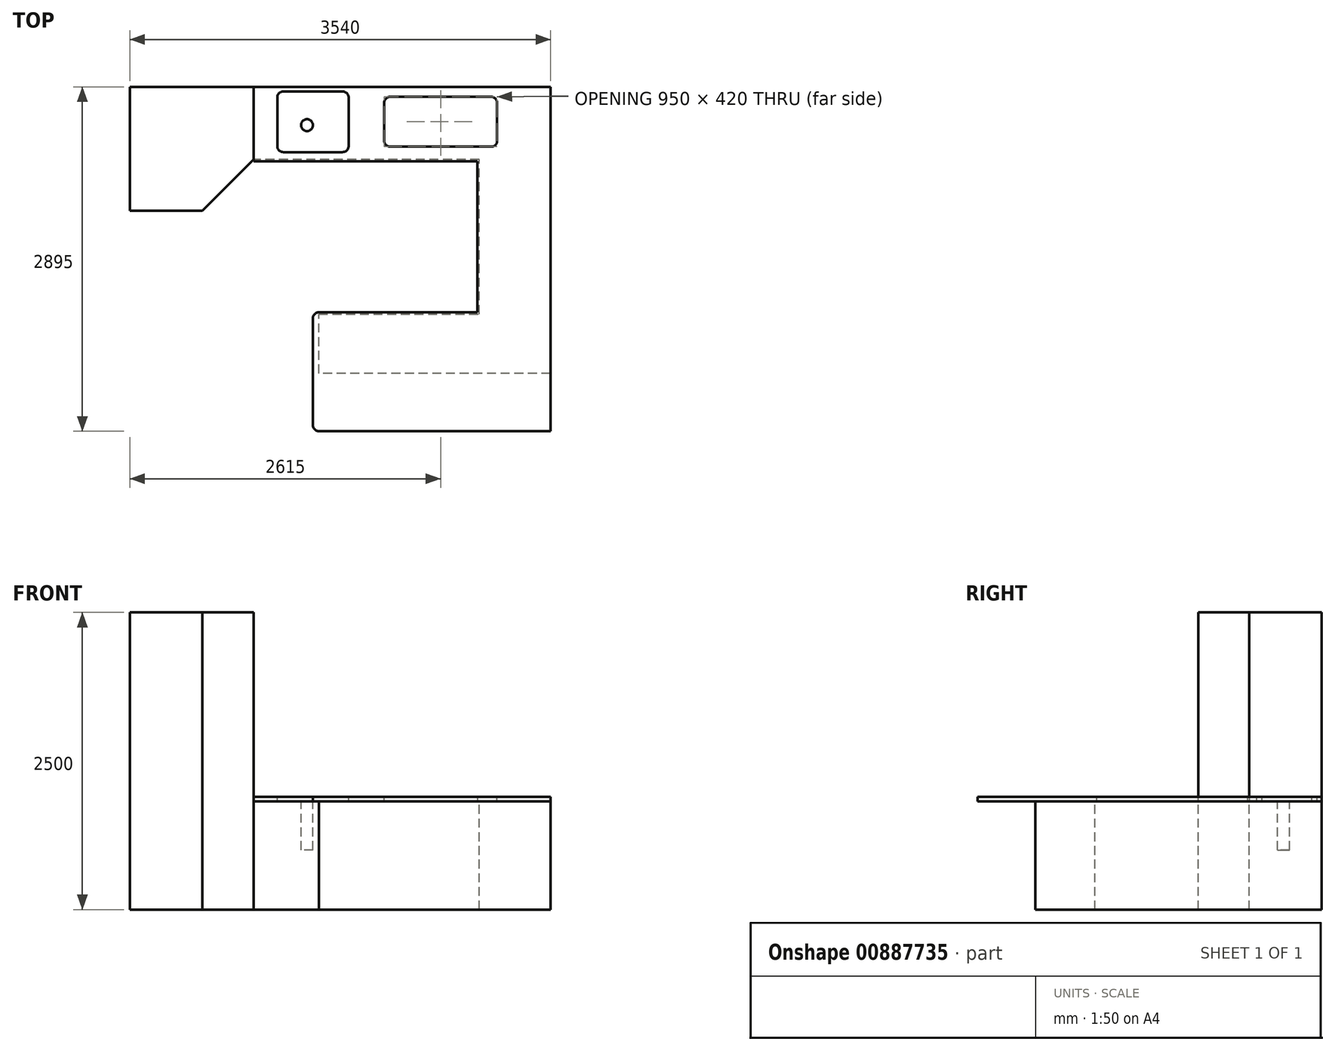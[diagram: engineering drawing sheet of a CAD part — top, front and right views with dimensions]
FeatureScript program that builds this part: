
annotation { "Feature Type Name" : "Feature", "Feature Type Description" : "" }
export const myFeature = defineFeature(function(context is Context, id is Id, definition is map)
    precondition{}
    {
        {
            var Q0;
            Q0=qCreatedBy(makeId("Top.planeOp"),FACE);
            var sketch = newSketch(context, id + "F0", { "sketchPlane" : qUnion([Q0])});
            skLineSegment(sketch, "E0.bottom", {"start": v(-624.7, -469.24) * mm, "end": v(415.3, -469.24) * mm});
            skLineSegment(sketch, "E0.top", {"start": v(-624.7, 570.76) * mm, "end": v(415.3, 570.76) * mm});
            skLineSegment(sketch, "E0.left", {"start": v(-624.7, -469.24) * mm, "end": v(-624.7, 570.76) * mm});
            skLineSegment(sketch, "E0.right", {"start": v(415.3, -469.24) * mm, "end": v(415.3, 570.76) * mm});
            skPoint(sketch, "E1.oppositeSnap0", {"position": v(-624.7, 50.76) * mm});
            skPoint(sketch, "E1.left.start.orphan", {"position": v(-624.7, 50.76) * mm});
            skSolve(sketch);
        }
        {
            var Q0;
            Q0 = qSketchRegion(id + "F0", true);
            extrude(context, id + "F1", {"entities" : qUnion([Q0]), "depth" : 2500 * mm, "offsetDistance" : 25 * mm});
        }
        {
            var Q0;
            Q0=makeQuery(id+"F1.opExtrude","SWEPT_EDGE",EDGE,{"disambiguationData":[OSD([sQuery(id+"F0.wireOp",EDGE,"E0.bottom"),sQuery(id+"F0.wireOp",EDGE,"E0.right")])]});
            chamfer(context, id + "F2", {"entities" : qUnion([Q0]), "width" : 430 * mm, "tangentPropagation" : true});
        }
        {
            var Q0;
            Q0=makeQuery(id+"F1.opExtrude","SWEPT_FACE",FACE,{"disambiguationData":[OSD([sQuery(id+"F0.wireOp",EDGE,"E0.right")])]});
            var sketch = newSketch(context, id + "F3", { "sketchPlane" : qUnion([Q0])});
            skLineSegment(sketch, "E2.bottom", {"start": v(570.76, 0) * mm, "end": v(-39.24, 0) * mm});
            skLineSegment(sketch, "E2.top", {"start": v(570.76, 910) * mm, "end": v(-39.24, 910) * mm});
            skLineSegment(sketch, "E2.left", {"start": v(570.76, 0) * mm, "end": v(570.76, 910) * mm});
            skLineSegment(sketch, "E2.right", {"start": v(-39.24, 0) * mm, "end": v(-39.24, 910) * mm});
            skSolve(sketch);
        }
        {
            var Q0;
            Q0=makeQuery(id+"F3.imprint","IMPRINT",FACE,{"disambiguationData":[TD([[makeQuery(id+"F3.imprint","IMPRINT",EDGE,{"derivedFrom":sQuery(id+"F3.wireOp",EDGE,"E2.bottom")}),1.0]])]});
            extrude(context, id + "F4", {"entities" : qUnion([Q0]), "operationType" : NewBodyOperationType.ADD, "depth" : 2500 * mm, "offsetDistance" : 25 * mm});
        }
        {
            var Q0;
            Q0=makeQuery(id+"F4.opExtrude","SWEPT_FACE",FACE,{"disambiguationData":[OSD([sQuery(id+"F3.wireOp",EDGE,"E2.right")])]});
            var sketch = newSketch(context, id + "F5", { "sketchPlane" : qUnion([Q0])});
            skLineSegment(sketch, "E3.bottom", {"start": v(2915.3, 0) * mm, "end": v(2315.3, 0) * mm});
            skLineSegment(sketch, "E3.top", {"start": v(2915.3, 910) * mm, "end": v(2315.3, 910) * mm});
            skLineSegment(sketch, "E3.left", {"start": v(2915.3, 0) * mm, "end": v(2915.3, 910) * mm});
            skLineSegment(sketch, "E3.right", {"start": v(2315.3, 0) * mm, "end": v(2315.3, 910) * mm});
            skSolve(sketch);
        }
        {
            var Q0;
            Q0=makeQuery(id+"F5.imprint","IMPRINT",FACE,{"disambiguationData":[TD([[makeQuery(id+"F5.imprint","IMPRINT",EDGE,{"derivedFrom":sQuery(id+"F5.wireOp",EDGE,"E3.bottom")}),-1.0]])]});
            extrude(context, id + "F6", {"entities" : qUnion([Q0]), "operationType" : NewBodyOperationType.ADD, "depth" : 1800 * mm, "offsetDistance" : 25 * mm});
        }
        {
            var Q0;
            Q0=makeQuery(id+"F6.opExtrude","SWEPT_FACE",FACE,{"disambiguationData":[OSD([sQuery(id+"F5.wireOp",EDGE,"E3.right")])]});
            var sketch = newSketch(context, id + "F7", { "sketchPlane" : qUnion([Q0])});
            skLineSegment(sketch, "E4.bottom", {"start": v(1839.24, 0) * mm, "end": v(1339.24, 0) * mm});
            skLineSegment(sketch, "E4.top", {"start": v(1839.24, 910) * mm, "end": v(1339.24, 910) * mm});
            skLineSegment(sketch, "E4.left", {"start": v(1839.24, 0) * mm, "end": v(1839.24, 910) * mm});
            skLineSegment(sketch, "E4.right", {"start": v(1339.24, 0) * mm, "end": v(1339.24, 910) * mm});
            skSolve(sketch);
        }
        {
            var Q0;
            Q0=makeQuery(id+"F7.imprint","IMPRINT",FACE,{"disambiguationData":[TD([[makeQuery(id+"F7.imprint","IMPRINT",EDGE,{"derivedFrom":sQuery(id+"F7.wireOp",EDGE,"E4.bottom")}),-1.0]])]});
            extrude(context, id + "F8", {"entities" : qUnion([Q0]), "operationType" : NewBodyOperationType.ADD, "depth" : 1400 * mm, "offsetDistance" : 25 * mm});
        }
        {
            var Q0;
            Q0=makeQuery(id+"F8.boolean.opBoolean","MERGE",FACE,{"derivedFrom":[makeQuery(id+"F6.boolean.opBoolean","MERGE",FACE,{"derivedFrom":[makeQuery(id+"F4.opExtrude","SWEPT_FACE",FACE,{"disambiguationData":[OSD([sQuery(id+"F3.wireOp",EDGE,"E2.top")])]}),makeQuery(id+"F6.opExtrude","SWEPT_FACE",FACE,{"disambiguationData":[OSD([sQuery(id+"F5.wireOp",EDGE,"E3.top")])]})]}),makeQuery(id+"F8.opExtrude","SWEPT_FACE",FACE,{"disambiguationData":[OSD([sQuery(id+"F7.wireOp",EDGE,"E4.top")])]})]});
            var sketch = newSketch(context, id + "F9", { "sketchPlane" : qUnion([Q0])});
            skLineSegment(sketch, "E5", {"start": v(2915.3, -1839.24) * mm, "end": v(2915.3, -2324.24) * mm});
            skLineSegment(sketch, "E6", {"start": v(2915.3, -2324.24) * mm, "end": v(915.3, -2324.24) * mm});
            skLineSegment(sketch, "E7", {"start": v(915.3, -2324.24) * mm, "end": v(915.3, -1339.24) * mm});
            skLineSegment(sketch, "E8", {"start": v(915.3, -1339.24) * mm, "end": v(915.3, -1324.24) * mm});
            skLineSegment(sketch, "E9", {"start": v(915.3, -1324.24) * mm, "end": v(2300.3, -1324.24) * mm});
            skLineSegment(sketch, "E10", {"start": v(2300.3, -1324.24) * mm, "end": v(2300.3, -54.24) * mm});
            skLineSegment(sketch, "E11", {"start": v(2300.3, -54.24) * mm, "end": v(415.3, -54.24) * mm});
            skLineSegment(sketch, "E12", {"start": v(415.3, -54.24) * mm, "end": v(415.3, 570.76) * mm});
            skLineSegment(sketch, "E13", {"start": v(415.3, 570.76) * mm, "end": v(2915.3, 570.76) * mm});
            skLineSegment(sketch, "E14", {"start": v(2915.3, 570.76) * mm, "end": v(2915.3, -1839.24) * mm});
            skSolve(sketch);
        }
        {
            var Q0;
            Q0 = qSketchRegion(id + "F9", true);
            extrude(context, id + "F10", {"entities" : qUnion([Q0]), "depth" : 38 * mm, "offsetDistance" : 25 * mm});
        }
        {
            var Q0;
            Q0=makeQuery(id+"F10.opExtrude","SWEPT_EDGE",EDGE,{"disambiguationData":[OSD([sQuery(id+"F9.wireOp",EDGE,"E8"),sQuery(id+"F9.wireOp",EDGE,"E9")])]});
            var Q1;
            Q1=makeQuery(id+"F10.opExtrude","SWEPT_EDGE",EDGE,{"disambiguationData":[OSD([sQuery(id+"F9.wireOp",EDGE,"E6"),sQuery(id+"F9.wireOp",EDGE,"E7")])]});
            fillet(context, id + "F11", {"entities" : qUnion([Q0, Q1]), "radius" : 50 * mm, "tangentPropagation" : true, "allowEdgeOverflow" : false});
        }
        {
            var Q0;
            Q0=makeQuery(id+"F8.opExtrude","CAP_FACE",FACE,{"disambiguationData":[OSD([sQuery(id+"F7.wireOp",EDGE,"E4.bottom"),sQuery(id+"F7.wireOp",EDGE,"E4.top"),sQuery(id+"F7.wireOp",EDGE,"E4.left"),sQuery(id+"F7.wireOp",EDGE,"E4.right")])],"isStart":false});
            var sketch = newSketch(context, id + "F12", { "sketchPlane" : qUnion([Q0])});
            skLineSegment(sketch, "E15.bottom", {"start": v(1839.24, 0) * mm, "end": v(1339.24, 0) * mm});
            skLineSegment(sketch, "E15.top", {"start": v(1839.24, 910) * mm, "end": v(1339.24, 910) * mm});
            skLineSegment(sketch, "E15.left", {"start": v(1839.24, 0) * mm, "end": v(1839.24, 910) * mm});
            skLineSegment(sketch, "E15.right", {"start": v(1339.24, 0) * mm, "end": v(1339.24, 910) * mm});
            skSolve(sketch);
        }
        {
            var Q0;
            Q0 = qSketchRegion(id + "F12", true);
            extrude(context, id + "F13", {"entities" : qUnion([Q0]), "operationType" : NewBodyOperationType.REMOVE, "oppositeDirection" : true, "depth" : 50 * mm, "offsetDistance" : 25 * mm});
        }
        {
            var Q0;
            Q0=makeQuery(id+"F8.boolean.opBoolean","MERGE",FACE,{"derivedFrom":[makeQuery(id+"F6.boolean.opBoolean","MERGE",FACE,{"derivedFrom":[makeQuery(id+"F4.opExtrude","SWEPT_FACE",FACE,{"disambiguationData":[OSD([sQuery(id+"F3.wireOp",EDGE,"E2.top")])]}),makeQuery(id+"F6.opExtrude","SWEPT_FACE",FACE,{"disambiguationData":[OSD([sQuery(id+"F5.wireOp",EDGE,"E3.top")])]})]}),makeQuery(id+"F8.opExtrude","SWEPT_FACE",FACE,{"disambiguationData":[OSD([sQuery(id+"F7.wireOp",EDGE,"E4.top")])]})]});
            var sketch = newSketch(context, id + "F14", { "sketchPlane" : qUnion([Q0])});
            skCircle(sketch, "E16", {"center": v(865.3, 250) * mm, "radius": 50 * mm});
            skSolve(sketch);
        }
        {
            var Q0;
            Q0=makeQuery(id+"F14.imprint","IMPRINT",FACE,{"disambiguationData":[TD([[makeQuery(id+"F14.imprint","IMPRINT",EDGE,{"derivedFrom":sQuery(id+"F14.wireOp",EDGE,"E16")}),1.0]])]});
            extrude(context, id + "F15", {"entities" : qUnion([Q0]), "operationType" : NewBodyOperationType.REMOVE, "oppositeDirection" : true, "depth" : 409 * mm, "offsetDistance" : 25 * mm});
        }
        {
            var Q0;
            Q0=makeQuery(id+"F10.opExtrude","CAP_FACE",FACE,{"disambiguationData":[OSD([sQuery(id+"F9.wireOp",EDGE,"E5"),sQuery(id+"F9.wireOp",EDGE,"E6"),sQuery(id+"F9.wireOp",EDGE,"E7"),sQuery(id+"F9.wireOp",EDGE,"E8"),sQuery(id+"F9.wireOp",EDGE,"E9"),sQuery(id+"F9.wireOp",EDGE,"E10"),sQuery(id+"F9.wireOp",EDGE,"E11"),sQuery(id+"F9.wireOp",EDGE,"E12"),sQuery(id+"F9.wireOp",EDGE,"E13"),sQuery(id+"F9.wireOp",EDGE,"E14")])],"isStart":false});
            var sketch = newSketch(context, id + "F16", { "sketchPlane" : qUnion([Q0])});
            skLineSegment(sketch, "E17.bottom", {"start": v(615.3, 533.26) * mm, "end": v(1215.3, 533.26) * mm});
            skLineSegment(sketch, "E17.top", {"start": v(615.3, 23.26) * mm, "end": v(1215.3, 23.26) * mm});
            skLineSegment(sketch, "E17.left", {"start": v(615.3, 533.26) * mm, "end": v(615.3, 23.26) * mm});
            skLineSegment(sketch, "E17.right", {"start": v(1215.3, 533.26) * mm, "end": v(1215.3, 23.26) * mm});
            skSolve(sketch);
        }
        {
            var Q0;
            Q0 = qSketchRegion(id + "F16", true);
            extrude(context, id + "F17", {"entities" : qUnion([Q0]), "operationType" : NewBodyOperationType.REMOVE, "oppositeDirection" : true, "depth" : 38 * mm, "offsetDistance" : 25 * mm});
        }
        {
            var Q0;
            Q0=makeQuery(id+"F17.boolean.opBoolean","COPY",EDGE,{"derivedFrom":makeQuery(id+"F17.opExtrude","SWEPT_EDGE",EDGE,{"disambiguationData":[OSD([sQuery(id+"F16.wireOp",EDGE,"E17.bottom"),sQuery(id+"F16.wireOp",EDGE,"E17.left")])]})});
            var Q1;
            Q1=makeQuery(id+"F17.boolean.opBoolean","COPY",EDGE,{"derivedFrom":makeQuery(id+"F17.opExtrude","SWEPT_EDGE",EDGE,{"disambiguationData":[OSD([sQuery(id+"F16.wireOp",EDGE,"E17.top"),sQuery(id+"F16.wireOp",EDGE,"E17.left")])]})});
            var Q2;
            Q2=makeQuery(id+"F17.boolean.opBoolean","COPY",EDGE,{"derivedFrom":makeQuery(id+"F17.opExtrude","SWEPT_EDGE",EDGE,{"disambiguationData":[OSD([sQuery(id+"F16.wireOp",EDGE,"E17.top"),sQuery(id+"F16.wireOp",EDGE,"E17.right")])]})});
            var Q3;
            Q3=makeQuery(id+"F17.boolean.opBoolean","COPY",EDGE,{"derivedFrom":makeQuery(id+"F17.opExtrude","SWEPT_EDGE",EDGE,{"disambiguationData":[OSD([sQuery(id+"F16.wireOp",EDGE,"E17.bottom"),sQuery(id+"F16.wireOp",EDGE,"E17.right")])]})});
            fillet(context, id + "F18", {"entities" : qUnion([Q0, Q1, Q2, Q3]), "radius" : 50 * mm, "tangentPropagation" : true, "allowEdgeOverflow" : false});
        }
        {
            var Q0;
            Q0=makeQuery(id+"F10.opExtrude","CAP_FACE",FACE,{"disambiguationData":[OSD([sQuery(id+"F9.wireOp",EDGE,"E5"),sQuery(id+"F9.wireOp",EDGE,"E6"),sQuery(id+"F9.wireOp",EDGE,"E7"),sQuery(id+"F9.wireOp",EDGE,"E8"),sQuery(id+"F9.wireOp",EDGE,"E9"),sQuery(id+"F9.wireOp",EDGE,"E10"),sQuery(id+"F9.wireOp",EDGE,"E11"),sQuery(id+"F9.wireOp",EDGE,"E12"),sQuery(id+"F9.wireOp",EDGE,"E13"),sQuery(id+"F9.wireOp",EDGE,"E14")])],"isStart":false});
            var sketch = newSketch(context, id + "F19", { "sketchPlane" : qUnion([Q0])});
            skLineSegment(sketch, "E18.bottom", {"start": v(1515.3, 488.26) * mm, "end": v(2465.3, 488.26) * mm});
            skLineSegment(sketch, "E18.top", {"start": v(1515.3, 68.26) * mm, "end": v(2465.3, 68.26) * mm});
            skLineSegment(sketch, "E18.left", {"start": v(1515.3, 488.26) * mm, "end": v(1515.3, 68.26) * mm});
            skLineSegment(sketch, "E18.right", {"start": v(2465.3, 488.26) * mm, "end": v(2465.3, 68.26) * mm});
            skSolve(sketch);
        }
        {
            var Q0;
            Q0 = qSketchRegion(id + "F19", true);
            extrude(context, id + "F20", {"entities" : qUnion([Q0]), "operationType" : NewBodyOperationType.REMOVE, "oppositeDirection" : true, "depth" : 38 * mm, "offsetDistance" : 25 * mm});
        }
        {
            var Q0;
            Q0=makeQuery(id+"F20.boolean.opBoolean","COPY",EDGE,{"derivedFrom":makeQuery(id+"F20.opExtrude","SWEPT_EDGE",EDGE,{"disambiguationData":[OSD([sQuery(id+"F19.wireOp",EDGE,"E18.bottom"),sQuery(id+"F19.wireOp",EDGE,"E18.left")])]})});
            var Q1;
            Q1=makeQuery(id+"F20.boolean.opBoolean","COPY",EDGE,{"derivedFrom":makeQuery(id+"F20.opExtrude","SWEPT_EDGE",EDGE,{"disambiguationData":[OSD([sQuery(id+"F19.wireOp",EDGE,"E18.bottom"),sQuery(id+"F19.wireOp",EDGE,"E18.right")])]})});
            var Q2;
            Q2=makeQuery(id+"F20.boolean.opBoolean","COPY",EDGE,{"derivedFrom":makeQuery(id+"F20.opExtrude","SWEPT_EDGE",EDGE,{"disambiguationData":[OSD([sQuery(id+"F19.wireOp",EDGE,"E18.top"),sQuery(id+"F19.wireOp",EDGE,"E18.left")])]})});
            var Q3;
            Q3=makeQuery(id+"F20.boolean.opBoolean","COPY",EDGE,{"derivedFrom":makeQuery(id+"F20.opExtrude","SWEPT_EDGE",EDGE,{"disambiguationData":[OSD([sQuery(id+"F19.wireOp",EDGE,"E18.top"),sQuery(id+"F19.wireOp",EDGE,"E18.right")])]})});
            fillet(context, id + "F21", {"entities" : qUnion([Q0, Q1, Q2, Q3]), "radius" : 50 * mm, "tangentPropagation" : true, "allowEdgeOverflow" : false});
        }
    });
